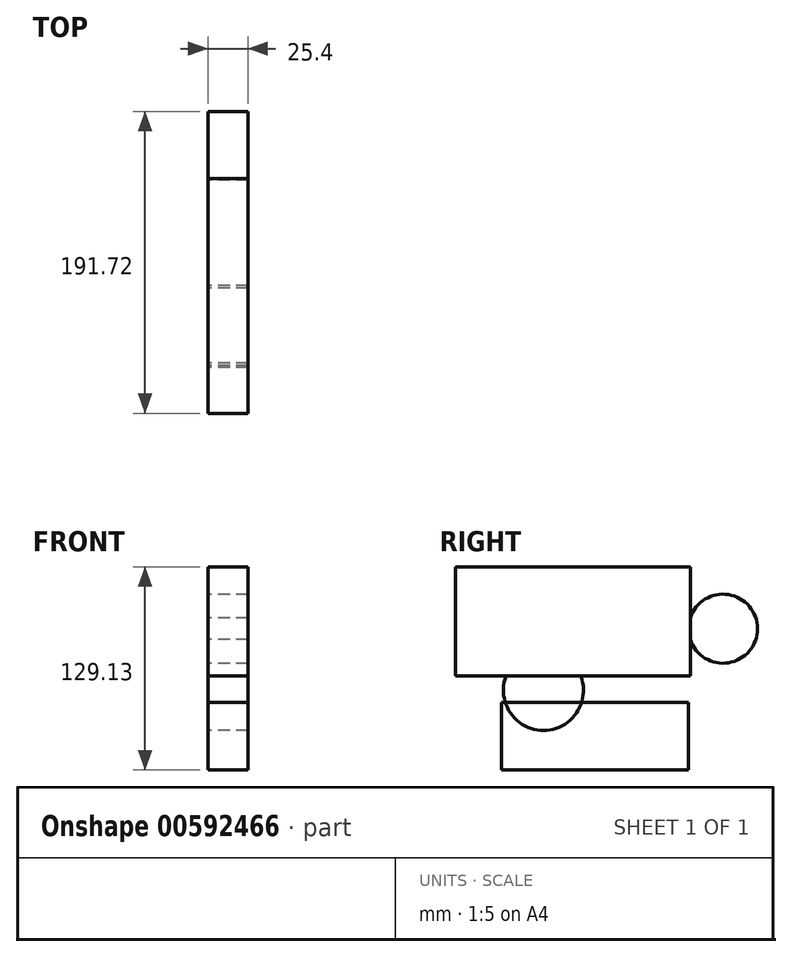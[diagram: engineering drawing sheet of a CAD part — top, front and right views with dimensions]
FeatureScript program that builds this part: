
annotation { "Feature Type Name" : "Feature", "Feature Type Description" : "" }
export const myFeature = defineFeature(function(context is Context, id is Id, definition is map)
    precondition{}
    {
        {
            var Q0;
            Q0=qCreatedBy(makeId("Right.planeOp"),FACE);
            var sketch = newSketch(context, id + "F0", { "sketchPlane" : qUnion([Q0])});
            skLineSegment(sketch, "E0.bottom", {"start": v(-63.06, 47.7) * mm, "end": v(85.95, 47.7) * mm});
            skLineSegment(sketch, "E0.top", {"start": v(-63.06, -21.75) * mm, "end": v(85.95, -21.75) * mm});
            skLineSegment(sketch, "E0.left", {"start": v(-63.06, 47.7) * mm, "end": v(-63.06, -21.75) * mm});
            skLineSegment(sketch, "E0.right", {"start": v(85.95, 47.7) * mm, "end": v(85.95, -21.75) * mm});
            skLineSegment(sketch, "E1.bottom", {"start": v(-33.85, -38.33) * mm, "end": v(84.98, -38.33) * mm});
            skLineSegment(sketch, "E1.top", {"start": v(-33.85, -81.43) * mm, "end": v(84.98, -81.43) * mm});
            skLineSegment(sketch, "E1.left", {"start": v(-33.85, -38.33) * mm, "end": v(-33.85, -81.43) * mm});
            skLineSegment(sketch, "E1.right", {"start": v(84.98, -38.33) * mm, "end": v(84.98, -81.43) * mm});
            skSolve(sketch);
        }
        {
            var Q0;
            Q0=makeQuery(id+"F0.imprint","IMPRINT",FACE,{"disambiguationData":[TD([[makeQuery(id+"F0.imprint","IMPRINT",EDGE,{"derivedFrom":sQuery(id+"F0.wireOp",EDGE,"E0.bottom")}),-1.0]])]});
            var sketch = newSketch(context, id + "F1", { "sketchPlane" : qUnion([Q0])});
            skCircle(sketch, "E2", {"center": v(106.74, 8.37) * mm, "radius": 21.92 * mm});
            skCircle(sketch, "E3", {"center": v(-7.27, -30.78) * mm, "radius": 25.43 * mm});
            skSolve(sketch);
        }
        {
            var Q0;
            {var subQ0=sQuery(id+"F1.wireOp",EDGE,"E2");var subQ1=makeQuery(id+"F0.imprint","IMPRINT",EDGE,{"derivedFrom":sQuery(id+"F0.wireOp",EDGE,"E0.right")});var subQ2=makeQuery(id+"F1.imprint","INTERSECT",VERTEX,{"disambiguationData":[OD(0.0)],"derivedFrom":[subQ1,subQ0]});Q0=makeQuery(id+"F1.imprint","IMPRINT",FACE,{"disambiguationData":[TD([[makeQuery(id+"F1.imprint","IMPRINT",EDGE,{"disambiguationData":[TD([[subQ2,1.0]])],"derivedFrom":subQ0}),1.0]])]});}
            var Q1;
            {var subQ0=sQuery(id+"F1.wireOp",EDGE,"E3");var subQ1=makeQuery(id+"F0.imprint","IMPRINT",EDGE,{"derivedFrom":sQuery(id+"F0.wireOp",EDGE,"E0.top")});var subQ2=makeQuery(id+"F1.imprint","INTERSECT",VERTEX,{"disambiguationData":[OD(0.0)],"derivedFrom":[subQ1,subQ0]});Q1=makeQuery(id+"F1.imprint","IMPRINT",FACE,{"disambiguationData":[TD([[makeQuery(id+"F1.imprint","IMPRINT",EDGE,{"disambiguationData":[TD([[subQ2,-1.0]])],"derivedFrom":subQ0}),1.0]])]});}
            var Q2;
            {var subQ0=sQuery(id+"F1.wireOp",EDGE,"E2");var subQ1=makeQuery(id+"F0.imprint","IMPRINT",EDGE,{"derivedFrom":sQuery(id+"F0.wireOp",EDGE,"E0.right")});var subQ2=makeQuery(id+"F1.imprint","INTERSECT",VERTEX,{"disambiguationData":[OD(0.0)],"derivedFrom":[subQ1,subQ0]});Q2=makeQuery(id+"F1.imprint","IMPRINT",FACE,{"disambiguationData":[TD([[makeQuery(id+"F1.imprint","IMPRINT",EDGE,{"disambiguationData":[TD([[subQ2,-1.0]])],"derivedFrom":subQ0}),1.0]])]});}
            var Q3;
            {var subQ0=sQuery(id+"F1.wireOp",EDGE,"E3");var subQ1=makeQuery(id+"F0.imprint","IMPRINT",EDGE,{"derivedFrom":sQuery(id+"F0.wireOp",EDGE,"E0.top")});var subQ2=makeQuery(id+"F1.imprint","INTERSECT",VERTEX,{"disambiguationData":[OD(0.0)],"derivedFrom":[subQ1,subQ0]});Q3=makeQuery(id+"F1.imprint","IMPRINT",FACE,{"disambiguationData":[TD([[makeQuery(id+"F1.imprint","IMPRINT",EDGE,{"disambiguationData":[TD([[subQ2,1.0]])],"derivedFrom":subQ0}),1.0]])]});}
            var Q4;
            Q4=makeQuery(id+"F0.imprint","IMPRINT",FACE,{"disambiguationData":[TD([[makeQuery(id+"F0.imprint","IMPRINT",EDGE,{"derivedFrom":sQuery(id+"F0.wireOp",EDGE,"E0.bottom")}),-1.0]])]});
            var Q5;
            {var subQ0=makeQuery(id+"F0.imprint","IMPRINT",EDGE,{"derivedFrom":sQuery(id+"F0.wireOp",EDGE,"E0.bottom")});Q5=makeQuery(id+"F1.imprint","IMPRINT",FACE,{"disambiguationData":[TD([[makeQuery(id+"F1.imprint","IMPRINT",EDGE,{"derivedFrom":subQ0}),-1.0]])]});}
            var Q6;
            Q6=makeQuery(id+"F0.imprint","IMPRINT",FACE,{"disambiguationData":[TD([[makeQuery(id+"F0.imprint","IMPRINT",EDGE,{"derivedFrom":sQuery(id+"F0.wireOp",EDGE,"E1.bottom")}),-1.0]])]});
            extrude(context, id + "F2", {"entities" : qUnion([Q0, Q1, Q2, Q3, Q4, Q5, Q6]), "depth" : 25.4 * mm, "offsetDistance" : 25.4 * mm});
        }
    });
